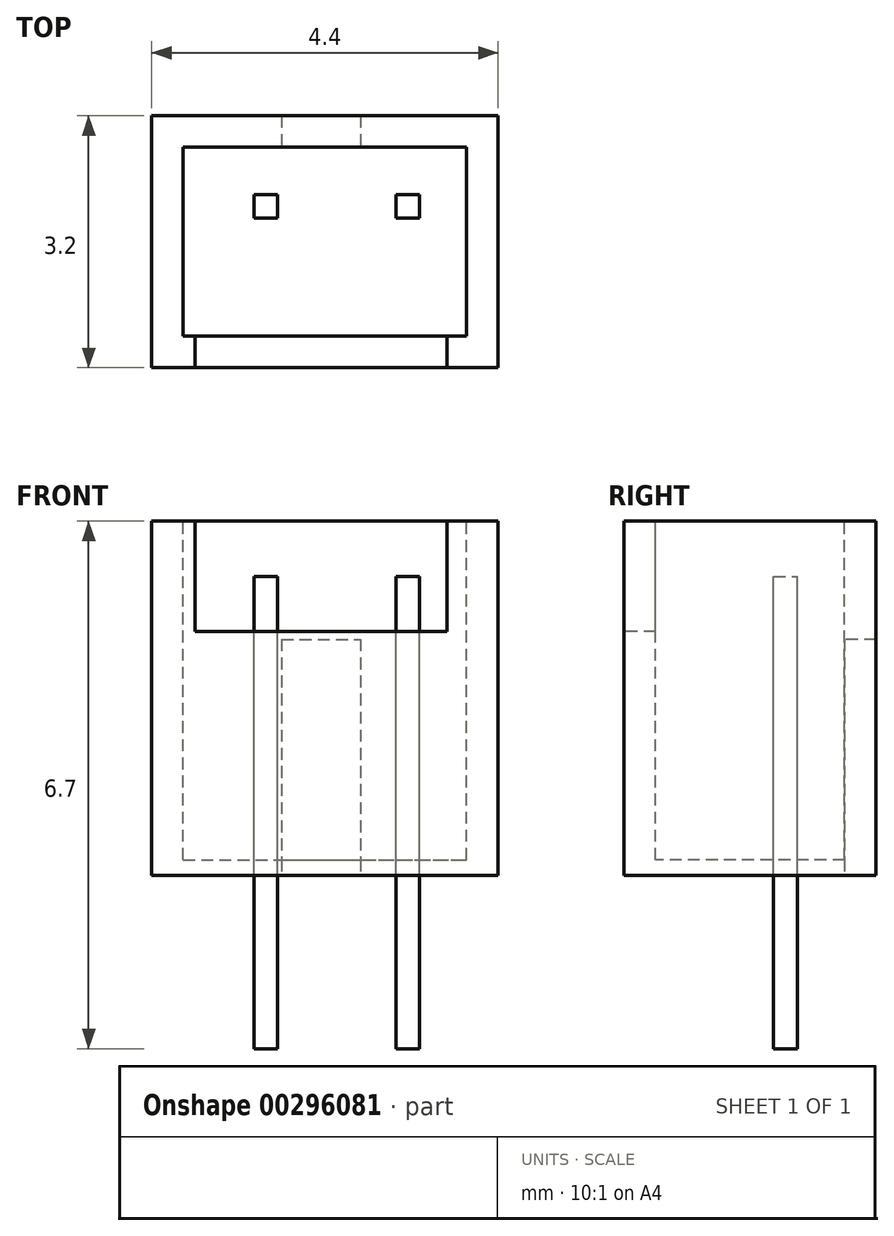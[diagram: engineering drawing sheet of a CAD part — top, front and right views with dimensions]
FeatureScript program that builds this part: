
annotation { "Feature Type Name" : "Feature", "Feature Type Description" : "" }
export const myFeature = defineFeature(function(context is Context, id is Id, definition is map)
    precondition{}
    {
        {
            var Q0;
            Q0=qCreatedBy(makeId("Top.planeOp"),FACE);
            var sketch = newSketch(context, id + "F0", { "sketchPlane" : qUnion([Q0])});
            skLineSegment(sketch, "E0.bottom", {"start": v(0, 0) * mm, "end": v(4.4, 0) * mm});
            skLineSegment(sketch, "E0.top", {"start": v(0, 3.2) * mm, "end": v(4.4, 3.2) * mm});
            skLineSegment(sketch, "E0.left", {"start": v(0, 0) * mm, "end": v(0, 3.2) * mm});
            skLineSegment(sketch, "E0.right", {"start": v(4.4, 0) * mm, "end": v(4.4, 3.2) * mm});
            skSolve(sketch);
        }
        {
            var Q0;
            Q0 = qSketchRegion(id + "F0", true);
            extrude(context, id + "F1", {"entities" : qUnion([Q0]), "depth" : 4.5 * mm});
        }
        {
            var Q0;
            Q0=makeQuery(id+"F1.opExtrude","CAP_FACE",FACE,{"disambiguationData":[OSD([sQuery(id+"F0.wireOp",EDGE,"E0.bottom"),sQuery(id+"F0.wireOp",EDGE,"E0.top"),sQuery(id+"F0.wireOp",EDGE,"E0.left"),sQuery(id+"F0.wireOp",EDGE,"E0.right")])],"isStart":false});
            var sketch = newSketch(context, id + "F2", { "sketchPlane" : qUnion([Q0])});
            skLineSegment(sketch, "E1.bottom", {"start": v(0.4, 2.8) * mm, "end": v(4, 2.8) * mm});
            skLineSegment(sketch, "E1.top", {"start": v(0.4, 0.4) * mm, "end": v(4, 0.4) * mm});
            skLineSegment(sketch, "E1.left", {"start": v(0.4, 2.8) * mm, "end": v(0.4, 0.4) * mm});
            skLineSegment(sketch, "E1.right", {"start": v(4, 2.8) * mm, "end": v(4, 0.4) * mm});
            skSolve(sketch);
        }
        {
            var Q0;
            Q0 = qSketchRegion(id + "F2", true);
            extrude(context, id + "F3", {"entities" : qUnion([Q0]), "operationType" : NewBodyOperationType.REMOVE, "oppositeDirection" : true, "depth" : 4.3 * mm});
        }
        {
            var Q0;
            Q0=makeQuery(id+"F1.opExtrude","CAP_FACE",FACE,{"disambiguationData":[OSD([sQuery(id+"F0.wireOp",EDGE,"E0.bottom"),sQuery(id+"F0.wireOp",EDGE,"E0.top"),sQuery(id+"F0.wireOp",EDGE,"E0.left"),sQuery(id+"F0.wireOp",EDGE,"E0.right")])],"isStart":false});
            var sketch = newSketch(context, id + "F4", { "sketchPlane" : qUnion([Q0])});
            skLineSegment(sketch, "E2.bottom", {"start": v(0.55, 0.4) * mm, "end": v(3.75, 0.4) * mm});
            skLineSegment(sketch, "E2.top", {"start": v(0.55, 0) * mm, "end": v(3.75, 0) * mm});
            skLineSegment(sketch, "E2.left", {"start": v(0.55, 0.4) * mm, "end": v(0.55, 0) * mm});
            skLineSegment(sketch, "E2.right", {"start": v(3.75, 0.4) * mm, "end": v(3.75, 0) * mm});
            skPoint(sketch, "E3", {"position": v(2.15, 0) * mm});
            skSolve(sketch);
        }
        {
            var Q0;
            Q0 = qSketchRegion(id + "F4", true);
            extrude(context, id + "F5", {"entities" : qUnion([Q0]), "operationType" : NewBodyOperationType.REMOVE, "oppositeDirection" : true, "depth" : 1.4 * mm});
        }
        {
            var Q0;
            Q0=makeQuery(id+"F1.opExtrude","CAP_FACE",FACE,{"disambiguationData":[OSD([sQuery(id+"F0.wireOp",EDGE,"E0.bottom"),sQuery(id+"F0.wireOp",EDGE,"E0.top"),sQuery(id+"F0.wireOp",EDGE,"E0.left"),sQuery(id+"F0.wireOp",EDGE,"E0.right")])],"isStart":true});
            var sketch = newSketch(context, id + "F6", { "sketchPlane" : qUnion([Q0])});
            skLineSegment(sketch, "E4.bottom", {"start": v(1.65, -3.2) * mm, "end": v(2.65, -3.2) * mm});
            skLineSegment(sketch, "E4.top", {"start": v(1.65, -2.8) * mm, "end": v(2.65, -2.8) * mm});
            skLineSegment(sketch, "E4.left", {"start": v(1.65, -3.2) * mm, "end": v(1.65, -2.8) * mm});
            skLineSegment(sketch, "E4.right", {"start": v(2.65, -3.2) * mm, "end": v(2.65, -2.8) * mm});
            skPoint(sketch, "E5", {"position": v(2.15, -3.2) * mm});
            skSolve(sketch);
        }
        {
            var Q0;
            Q0 = qSketchRegion(id + "F6", true);
            extrude(context, id + "F7", {"entities" : qUnion([Q0]), "operationType" : NewBodyOperationType.REMOVE, "oppositeDirection" : true, "depth" : 3 * mm});
        }
        {
            var Q0;
            Q0=makeQuery(id+"F1.opExtrude","CAP_FACE",FACE,{"disambiguationData":[OSD([sQuery(id+"F0.wireOp",EDGE,"E0.bottom"),sQuery(id+"F0.wireOp",EDGE,"E0.top"),sQuery(id+"F0.wireOp",EDGE,"E0.left"),sQuery(id+"F0.wireOp",EDGE,"E0.right")])],"isStart":true});
            var sketch = newSketch(context, id + "F8", { "sketchPlane" : qUnion([Q0])});
            skLineSegment(sketch, "E6.bottom", {"start": v(1.3, -1.9) * mm, "end": v(1.6, -1.9) * mm});
            skLineSegment(sketch, "E6.top", {"start": v(1.3, -2.2) * mm, "end": v(1.6, -2.2) * mm});
            skLineSegment(sketch, "E6.left", {"start": v(1.3, -1.9) * mm, "end": v(1.3, -2.2) * mm});
            skLineSegment(sketch, "E6.right", {"start": v(1.6, -1.9) * mm, "end": v(1.6, -2.2) * mm});
            skLineSegment(sketch, "E7.bottom", {"start": v(3.1, -1.9) * mm, "end": v(3.4, -1.9) * mm});
            skLineSegment(sketch, "E7.top", {"start": v(3.1, -2.2) * mm, "end": v(3.4, -2.2) * mm});
            skLineSegment(sketch, "E7.left", {"start": v(3.4, -1.9) * mm, "end": v(3.4, -2.2) * mm});
            skLineSegment(sketch, "E7.right", {"start": v(3.1, -1.9) * mm, "end": v(3.1, -2.2) * mm});
            skSolve(sketch);
        }
        {
            var Q0;
            Q0 = qSketchRegion(id + "F8", true);
            extrude(context, id + "F9", {"entities" : qUnion([Q0]), "depth" : 2.2 * mm, "hasSecondDirection" : true, "secondDirectionOppositeDirection" : true, "secondDirectionDepth" : 3.8 * mm});
        }
    });
